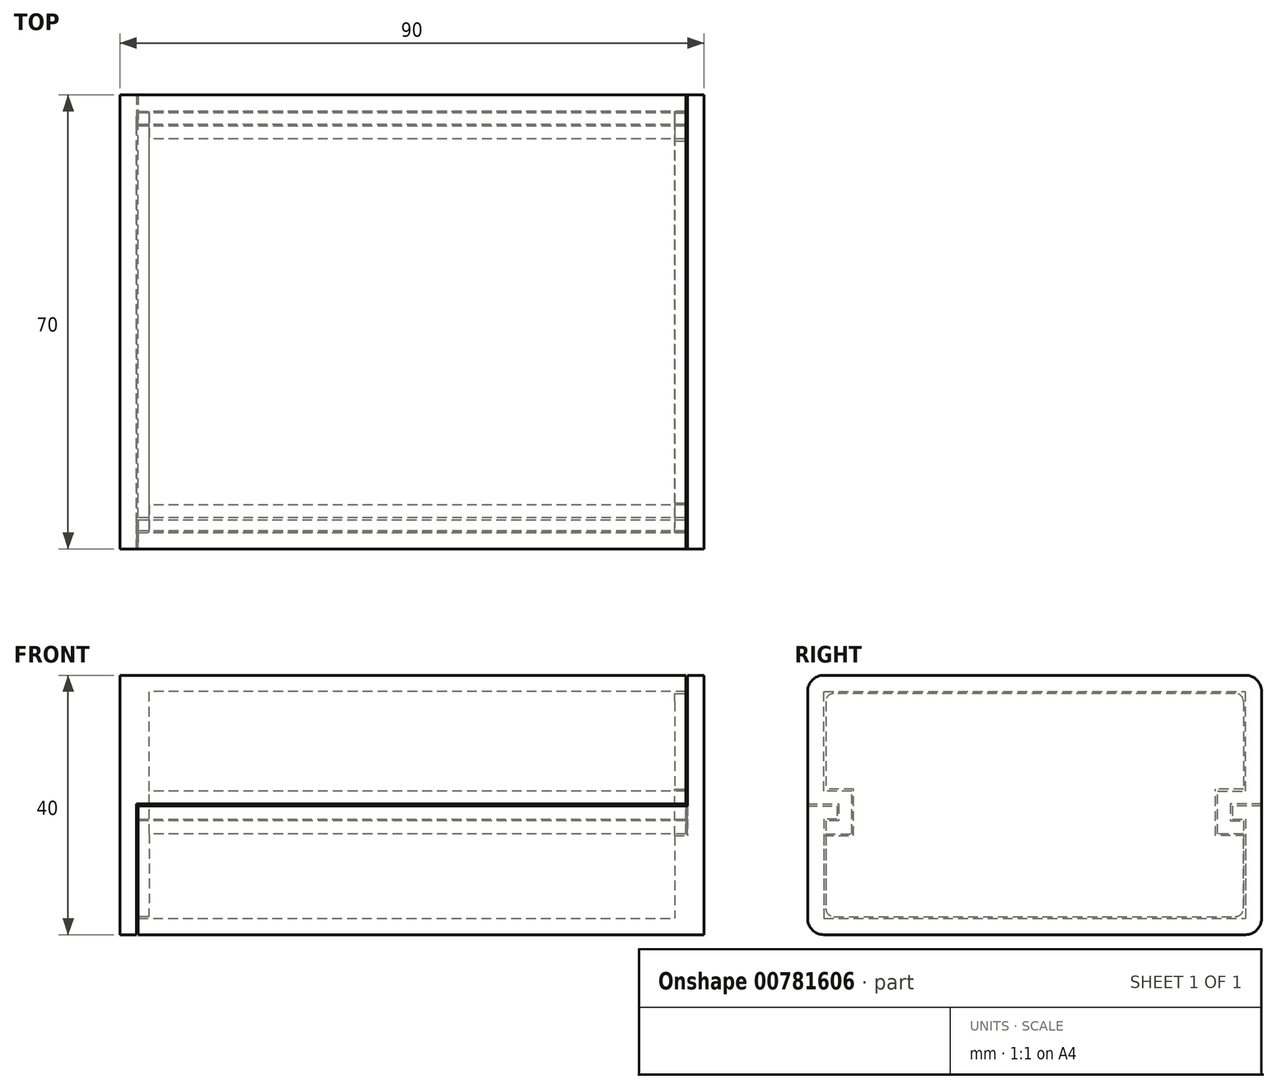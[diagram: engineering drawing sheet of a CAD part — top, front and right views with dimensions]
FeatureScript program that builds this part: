
annotation { "Feature Type Name" : "Feature", "Feature Type Description" : "" }
export const myFeature = defineFeature(function(context is Context, id is Id, definition is map)
    precondition{}
    {
        {
            assignVariable(context, id + "F0", {"name" : "LipSize", "anyValue" : 2});
        }
        {
            assignVariable(context, id + "F1", {"name" : "Thickness", "anyValue" : 2.5});
        }
        {
            var Q0;
            Q0=qCreatedBy(makeId("Top.planeOp"),FACE);
            var sketch = newSketch(context, id + "F2", { "sketchPlane" : qUnion([Q0])});
            skLineSegment(sketch, "E0.bottom", {"start": v(-45, 35) * mm, "end": v(45, 35) * mm});
            skLineSegment(sketch, "E0.top", {"start": v(-45, -35) * mm, "end": v(45, -35) * mm});
            skLineSegment(sketch, "E0.left", {"start": v(-45, 35) * mm, "end": v(-45, -35) * mm});
            skLineSegment(sketch, "E0.right", {"start": v(45, 35) * mm, "end": v(45, -35) * mm});
            skLineSegment(sketch, "E1", {"start": v(-42.5, 35) * mm, "end": v(-42.5, -35) * mm, "construction": true});
            skLineSegment(sketch, "E2", {"start": v(42.5, 35) * mm, "end": v(42.5, -35) * mm, "construction": true});
            skLineSegment(sketch, "E3", {"start": v(42.2, 35) * mm, "end": v(42.2, -35) * mm, "construction": true});
            skLineSegment(sketch, "E4", {"start": v(-42.2, 35) * mm, "end": v(-42.2, -35) * mm, "construction": true});
            skSolve(sketch);
        }
        {
            var Q0;
            Q0=qCreatedBy(makeId("Right.planeOp"),FACE);
            var sketch = newSketch(context, id + "F3", { "sketchPlane" : qUnion([Q0])});
            skLineSegment(sketch, "E5.bottom", {"start": v(-35, 20) * mm, "end": v(35, 20) * mm});
            skLineSegment(sketch, "E5.top", {"start": v(-35, -20) * mm, "end": v(35, -20) * mm});
            skLineSegment(sketch, "E5.left", {"start": v(-35, 20) * mm, "end": v(-35, -20) * mm});
            skLineSegment(sketch, "E5.right", {"start": v(35, 20) * mm, "end": v(35, -20) * mm});
            skLineSegment(sketch, "E6", {"start": v(-35, 0) * mm, "end": v(35, 0) * mm, "construction": true});
            skLineSegment(sketch, "E7", {"start": v(35, 17.5) * mm, "end": v(-35, 17.5) * mm, "construction": true});
            skLineSegment(sketch, "E8", {"start": v(35, 17.2) * mm, "end": v(-35, 17.2) * mm, "construction": true});
            skLineSegment(sketch, "E9", {"start": v(35, -17.5) * mm, "end": v(-35, -17.5) * mm, "construction": true});
            skLineSegment(sketch, "E10", {"start": v(-35, -17.2) * mm, "end": v(35, -17.2) * mm, "construction": true});
            skLineSegment(sketch, "E11", {"start": v(32.5, 17.5) * mm, "end": v(32.5, -17.5) * mm, "construction": true});
            skLineSegment(sketch, "E12", {"start": v(-32.5, 17.5) * mm, "end": v(-32.5, -17.5) * mm, "construction": true});
            skSolve(sketch);
        }
        {
            var Q0;
            Q0=makeQuery(id+"F3.imprint","IMPRINT",FACE,{"disambiguationData":[TD([[makeQuery(id+"F3.imprint","IMPRINT",EDGE,{"derivedFrom":sQuery(id+"F3.wireOp",EDGE,"E5.bottom")}),-1.0]])]});
            var sketch = newSketch(context, id + "F4", { "sketchPlane" : qUnion([Q0])});
            skLineSegment(sketch, "E13", {"start": v(-35, -0.15) * mm, "end": v(-35, -20) * mm});
            skLineSegment(sketch, "E14.0", {"start": v(-35, -20) * mm, "end": v(35, -20) * mm});
            skLineSegment(sketch, "E15.0", {"start": v(-35, 20) * mm, "end": v(35, 20) * mm});
            skLineSegment(sketch, "E16", {"start": v(-35, 20) * mm, "end": v(-35, 0.15) * mm});
            skLineSegment(sketch, "E17", {"start": v(35, 20) * mm, "end": v(35, 0.15) * mm});
            skLineSegment(sketch, "E18", {"start": v(35, -20) * mm, "end": v(35, -0.15) * mm});
            skLineSegment(sketch, "E19", {"start": v(-35, -0.15) * mm, "end": v(-30.5, -0.15) * mm});
            skLineSegment(sketch, "E20", {"start": v(-30.5, -0.15) * mm, "end": v(-30.5, -2.15) * mm});
            skLineSegment(sketch, "E21", {"start": v(-30.5, -2.15) * mm, "end": v(-32.5, -2.15) * mm});
            skLineSegment(sketch, "E22", {"start": v(-32.5, -2.15) * mm, "end": v(-32.5, -17.5) * mm});
            skLineSegment(sketch, "E23", {"start": v(0, 20) * mm, "end": v(0, -20) * mm, "construction": true});
            skLineSegment(sketch, "E24", {"start": v(-32.5, -17.5) * mm, "end": v(32.5, -17.5) * mm});
            skLineSegment(sketch, "E25", {"start": v(-35, 0.15) * mm, "end": v(-30.2, 0.15) * mm});
            skLineSegment(sketch, "E26", {"start": v(-30.2, 0.15) * mm, "end": v(-30.2, -2.45) * mm});
            skLineSegment(sketch, "E27", {"start": v(-30.2, -2.45) * mm, "end": v(-32.2, -2.45) * mm});
            skLineSegment(sketch, "E28", {"start": v(-32.2, -2.45) * mm, "end": v(-32.2, -4.45) * mm});
            skLineSegment(sketch, "E29", {"start": v(-32.2, -4.45) * mm, "end": v(-28.2, -4.45) * mm});
            skLineSegment(sketch, "E30", {"start": v(-28.2, -4.45) * mm, "end": v(-28.2, 2.15) * mm});
            skLineSegment(sketch, "E31", {"start": v(-28.2, 2.15) * mm, "end": v(-32.5, 2.15) * mm});
            skLineSegment(sketch, "E32", {"start": v(-32.5, 2.15) * mm, "end": v(-32.5, 17.5) * mm});
            skLineSegment(sketch, "E33", {"start": v(-32.5, 17.5) * mm, "end": v(32.5, 17.5) * mm});
            skLineSegment(sketch, "E34.MirrorCS", {"start": v(35, -0.15) * mm, "end": v(35, -20) * mm});
            skLineSegment(sketch, "E35.MirrorCS", {"start": v(32.2, -4.45) * mm, "end": v(28.2, -4.45) * mm});
            skLineSegment(sketch, "E36.MirrorCS", {"start": v(32.2, -2.45) * mm, "end": v(32.2, -4.45) * mm});
            skLineSegment(sketch, "E37.MirrorCS", {"start": v(32.5, -2.15) * mm, "end": v(32.5, -17.5) * mm});
            skLineSegment(sketch, "E38.MirrorCS", {"start": v(28.2, 2.15) * mm, "end": v(32.5, 2.15) * mm});
            skLineSegment(sketch, "E39.MirrorCS", {"start": v(30.2, -2.45) * mm, "end": v(32.2, -2.45) * mm});
            skLineSegment(sketch, "E40.MirrorCS", {"start": v(35, -0.15) * mm, "end": v(30.5, -0.15) * mm});
            skLineSegment(sketch, "E41.MirrorCS", {"start": v(30.5, -2.15) * mm, "end": v(32.5, -2.15) * mm});
            skLineSegment(sketch, "E42.MirrorCS", {"start": v(35, 0.15) * mm, "end": v(30.2, 0.15) * mm});
            skLineSegment(sketch, "E43.MirrorCS", {"start": v(30.5, -0.15) * mm, "end": v(30.5, -2.15) * mm});
            skLineSegment(sketch, "E44.MirrorCS", {"start": v(30.2, 0.15) * mm, "end": v(30.2, -2.45) * mm});
            skLineSegment(sketch, "E45.MirrorCS", {"start": v(32.5, 2.15) * mm, "end": v(32.5, 17.5) * mm});
            skLineSegment(sketch, "E46.MirrorCS", {"start": v(28.2, -4.45) * mm, "end": v(28.2, 2.15) * mm});
            skSolve(sketch);
        }
        {
            var Q0;
            Q0=makeQuery(id+"F4.imprint","IMPRINT",FACE,{"disambiguationData":[TD([[makeQuery(id+"F4.imprint","IMPRINT",EDGE,{"derivedFrom":sQuery(id+"F4.wireOp",EDGE,"E15.0")}),-1.0]])]});
            var Q1;
            Q1=sQuery(id+"F2.wireOp",VERTEX,"E3.end");
            var Q2;
            Q2=sQuery(id+"F2.wireOp",VERTEX,"E1.end");
            extrude(context, id + "F5", {"entities" : qUnion([Q0]), "endBound" : BoundingType.UP_TO_VERTEX, "depth" : 25 * mm, "endBoundEntityVertex" : qUnion([Q1]), "offsetDistance" : 25 * mm, "hasSecondDirection" : true, "secondDirectionBound" : BoundingType.UP_TO_VERTEX, "secondDirectionOppositeDirection" : true, "secondDirectionDepth" : 25 * mm, "secondDirectionBoundEntityVertex" : qUnion([Q2])});
        }
        {
            var Q0;
            Q0=makeQuery(id+"F4.imprint","IMPRINT",FACE,{"disambiguationData":[TD([[makeQuery(id+"F4.imprint","IMPRINT",EDGE,{"derivedFrom":sQuery(id+"F4.wireOp",EDGE,"E13")}),1.0]])]});
            var Q1;
            Q1=sQuery(id+"F2.wireOp",VERTEX,"E4.end");
            var Q2;
            Q2=sQuery(id+"F2.wireOp",VERTEX,"E2.end");
            extrude(context, id + "F6", {"entities" : qUnion([Q0]), "endBound" : BoundingType.UP_TO_VERTEX, "oppositeDirection" : true, "depth" : 25 * mm, "endBoundEntityVertex" : qUnion([Q1]), "offsetDistance" : 25 * mm, "hasSecondDirection" : true, "secondDirectionBound" : BoundingType.UP_TO_VERTEX, "secondDirectionOppositeDirection" : false, "secondDirectionDepth" : 25 * mm, "secondDirectionBoundEntityVertex" : qUnion([Q2])});
        }
        {
            var Q0;
            Q0=makeQuery(id+"F5.opExtrude","CAP_FACE",FACE,{"disambiguationData":[OSD([sQuery(id+"F4.wireOp",EDGE,"E15.0"),sQuery(id+"F4.wireOp",EDGE,"E16"),sQuery(id+"F4.wireOp",EDGE,"E25"),sQuery(id+"F4.wireOp",EDGE,"E26"),sQuery(id+"F4.wireOp",EDGE,"E27"),sQuery(id+"F4.wireOp",EDGE,"E28"),sQuery(id+"F4.wireOp",EDGE,"E29"),sQuery(id+"F4.wireOp",EDGE,"E30"),sQuery(id+"F4.wireOp",EDGE,"E31"),sQuery(id+"F4.wireOp",EDGE,"E32"),sQuery(id+"F4.wireOp",EDGE,"E33"),sQuery(id+"F4.wireOp",EDGE,"E17"),sQuery(id+"F4.wireOp",EDGE,"E35.MirrorCS"),sQuery(id+"F4.wireOp",EDGE,"E36.MirrorCS"),sQuery(id+"F4.wireOp",EDGE,"E38.MirrorCS"),sQuery(id+"F4.wireOp",EDGE,"E39.MirrorCS"),sQuery(id+"F4.wireOp",EDGE,"E42.MirrorCS"),sQuery(id+"F4.wireOp",EDGE,"E44.MirrorCS"),sQuery(id+"F4.wireOp",EDGE,"E45.MirrorCS"),sQuery(id+"F4.wireOp",EDGE,"E46.MirrorCS")])],"isStart":true});
            var sketch = newSketch(context, id + "F7", { "sketchPlane" : qUnion([Q0])});
            skLineSegment(sketch, "E47.bottom", {"start": v(-35, 20) * mm, "end": v(35, 20) * mm});
            skLineSegment(sketch, "E47.top", {"start": v(-35, -20) * mm, "end": v(35, -20) * mm});
            skLineSegment(sketch, "E47.left", {"start": v(-35, 20) * mm, "end": v(-35, -20) * mm});
            skLineSegment(sketch, "E47.right", {"start": v(35, 20) * mm, "end": v(35, -20) * mm});
            skSolve(sketch);
        }
        {
            var Q0;
            Q0 = qSketchRegion(id + "F7", true);
            var Q1;
            Q1=sQuery(id+"F2.wireOp",VERTEX,"E0.bottom.start");
            extrude(context, id + "F8", {"entities" : qUnion([Q0]), "operationType" : NewBodyOperationType.ADD, "endBound" : BoundingType.UP_TO_VERTEX, "depth" : 25 * mm, "endBoundEntityVertex" : qUnion([Q1]), "offsetDistance" : 25 * mm});
        }
        {
            var Q0;
            Q0=makeQuery(id+"F6.opExtrude","CAP_FACE",FACE,{"disambiguationData":[OSD([sQuery(id+"F4.wireOp",EDGE,"E13"),sQuery(id+"F4.wireOp",EDGE,"E14.0"),sQuery(id+"F4.wireOp",EDGE,"E19"),sQuery(id+"F4.wireOp",EDGE,"E20"),sQuery(id+"F4.wireOp",EDGE,"E21"),sQuery(id+"F4.wireOp",EDGE,"E22"),sQuery(id+"F4.wireOp",EDGE,"E24"),sQuery(id+"F4.wireOp",EDGE,"E34.MirrorCS"),sQuery(id+"F4.wireOp",EDGE,"E37.MirrorCS"),sQuery(id+"F4.wireOp",EDGE,"E40.MirrorCS"),sQuery(id+"F4.wireOp",EDGE,"E41.MirrorCS"),sQuery(id+"F4.wireOp",EDGE,"E43.MirrorCS")])],"isStart":true});
            var sketch = newSketch(context, id + "F9", { "sketchPlane" : qUnion([Q0])});
            skLineSegment(sketch, "E48.bottom", {"start": v(35, -20) * mm, "end": v(-35, -20) * mm});
            skLineSegment(sketch, "E48.top", {"start": v(35, 20) * mm, "end": v(-35, 20) * mm});
            skLineSegment(sketch, "E48.left", {"start": v(35, -20) * mm, "end": v(35, 20) * mm});
            skLineSegment(sketch, "E48.right", {"start": v(-35, -20) * mm, "end": v(-35, 20) * mm});
            skSolve(sketch);
        }
        {
            var Q0;
            Q0 = qSketchRegion(id + "F9", true);
            var Q1;
            Q1=sQuery(id+"F2.wireOp",VERTEX,"E0.top.end");
            extrude(context, id + "F10", {"entities" : qUnion([Q0]), "operationType" : NewBodyOperationType.ADD, "endBound" : BoundingType.UP_TO_VERTEX, "depth" : 25 * mm, "endBoundEntityVertex" : qUnion([Q1]), "offsetDistance" : 25 * mm});
        }
        {
            var Q0;
            Q0=makeQuery(id+"F8.opExtrude","CAP_FACE",FACE,{"disambiguationData":[OSD([sQuery(id+"F7.wireOp",EDGE,"E47.bottom"),sQuery(id+"F7.wireOp",EDGE,"E47.top"),sQuery(id+"F7.wireOp",EDGE,"E47.left"),sQuery(id+"F7.wireOp",EDGE,"E47.right")])],"isStart":true});
            var sketch = newSketch(context, id + "F11", { "sketchPlane" : qUnion([Q0])});
            skLineSegment(sketch, "E49", {"start": v(-32.2, -4.45) * mm, "end": v(-32.2, -17.2) * mm});
            skLineSegment(sketch, "E50", {"start": v(-32.2, -17.2) * mm, "end": v(32.2, -17.2) * mm});
            skLineSegment(sketch, "E51", {"start": v(32.2, -17.2) * mm, "end": v(32.2, -4.45) * mm});
            skSolve(sketch);
        }
        {
            var Q0;
            Q0=makeQuery(id+"F11.imprint","IMPRINT",FACE,{"disambiguationData":[TD([[makeQuery(id+"F11.imprint","IMPRINT",EDGE,{"derivedFrom":sQuery(id+"F11.wireOp",EDGE,"E49")}),1.0]])]});
            extrude(context, id + "F12", {"entities" : qUnion([Q0]), "operationType" : NewBodyOperationType.ADD, "depth" : (getVariable(context, 'LipSize')) * mm, "offsetDistance" : 25 * mm});
        }
        {
            var Q0;
            Q0=makeQuery(id+"F10.opExtrude","CAP_FACE",FACE,{"disambiguationData":[OSD([sQuery(id+"F9.wireOp",EDGE,"E48.bottom"),sQuery(id+"F9.wireOp",EDGE,"E48.top"),sQuery(id+"F9.wireOp",EDGE,"E48.left"),sQuery(id+"F9.wireOp",EDGE,"E48.right")])],"isStart":true});
            var sketch = newSketch(context, id + "F13", { "sketchPlane" : qUnion([Q0])});
            skLineSegment(sketch, "E52.bottom", {"start": v(-32.2, 17.2) * mm, "end": v(32.2, 17.2) * mm});
            skLineSegment(sketch, "E52.top", {"start": v(-32.2, 2.45) * mm, "end": v(-27.9, 2.45) * mm});
            skLineSegment(sketch, "E52.left", {"start": v(-32.2, 17.2) * mm, "end": v(-32.2, 2.45) * mm});
            skLineSegment(sketch, "E52.right", {"start": v(32.2, 17.2) * mm, "end": v(32.2, 2.45) * mm});
            skLineSegment(sketch, "E53", {"start": v(-32.5, -4.75) * mm, "end": v(-27.9, -4.75) * mm});
            skLineSegment(sketch, "E54", {"start": v(-27.9, -4.75) * mm, "end": v(-27.9, 2.45) * mm});
            skLineSegment(sketch, "E55.MirrorCS", {"start": v(27.9, -4.75) * mm, "end": v(27.9, 2.45) * mm});
            skLineSegment(sketch, "E56.MirrorCS", {"start": v(32.5, -4.75) * mm, "end": v(27.9, -4.75) * mm});
            skLineSegment(sketch, "E57.trimOffspring", {"start": v(27.9, 2.45) * mm, "end": v(32.2, 2.45) * mm});
            skSolve(sketch);
        }
        {
            var Q0;
            Q0=makeQuery(id+"F13.imprint","IMPRINT",FACE,{"disambiguationData":[TD([[makeQuery(id+"F13.imprint","IMPRINT",EDGE,{"derivedFrom":sQuery(id+"F13.wireOp",EDGE,"E52.bottom")}),-1.0]])]});
            extrude(context, id + "F14", {"entities" : qUnion([Q0]), "operationType" : NewBodyOperationType.ADD, "depth" : (getVariable(context, 'LipSize')) * mm, "offsetDistance" : 25 * mm});
        }
        {
            var Q0;
            Q0=makeQuery(id+"F8.boolean.opBoolean","MERGE",EDGE,{"derivedFrom":[makeQuery(id+"F5.opExtrude","TWEAK_EDGE",EDGE,{"derivedFrom":[makeQuery(id+"F4.imprint","IMPRINT",EDGE,{"derivedFrom":sQuery(id+"F4.wireOp",EDGE,"E15.0")}),makeQuery(id+"F4.imprint","IMPRINT",EDGE,{"derivedFrom":sQuery(id+"F4.wireOp",EDGE,"E16")})]}),makeQuery(id+"F8.opExtrude","SWEPT_EDGE",EDGE,{"disambiguationData":[OSD([sQuery(id+"F7.wireOp",EDGE,"E47.bottom"),sQuery(id+"F7.wireOp",EDGE,"E47.right")])]})]});
            var Q1;
            Q1=makeQuery(id+"F8.boolean.opBoolean","MERGE",EDGE,{"derivedFrom":[makeQuery(id+"F5.opExtrude","TWEAK_EDGE",EDGE,{"derivedFrom":[makeQuery(id+"F4.imprint","IMPRINT",EDGE,{"derivedFrom":sQuery(id+"F4.wireOp",EDGE,"E15.0")}),makeQuery(id+"F4.imprint","IMPRINT",EDGE,{"derivedFrom":sQuery(id+"F4.wireOp",EDGE,"E17")})]}),makeQuery(id+"F8.opExtrude","SWEPT_EDGE",EDGE,{"disambiguationData":[OSD([sQuery(id+"F7.wireOp",EDGE,"E47.bottom"),sQuery(id+"F7.wireOp",EDGE,"E47.left")])]})]});
            var Q2;
            Q2=makeQuery(id+"F10.boolean.opBoolean","MERGE",EDGE,{"derivedFrom":[makeQuery(id+"F6.opExtrude","TWEAK_EDGE",EDGE,{"derivedFrom":[makeQuery(id+"F4.imprint","IMPRINT",EDGE,{"derivedFrom":sQuery(id+"F4.wireOp",EDGE,"E13")}),makeQuery(id+"F4.imprint","IMPRINT",EDGE,{"derivedFrom":sQuery(id+"F4.wireOp",EDGE,"E14.0")})]}),makeQuery(id+"F10.opExtrude","SWEPT_EDGE",EDGE,{"disambiguationData":[OSD([sQuery(id+"F9.wireOp",EDGE,"E48.bottom"),sQuery(id+"F9.wireOp",EDGE,"E48.right")])]})]});
            var Q3;
            Q3=makeQuery(id+"F8.opExtrude","SWEPT_EDGE",EDGE,{"disambiguationData":[OSD([sQuery(id+"F7.wireOp",EDGE,"E47.top"),sQuery(id+"F7.wireOp",EDGE,"E47.right")])]});
            var Q4;
            Q4=makeQuery(id+"F10.opExtrude","SWEPT_EDGE",EDGE,{"disambiguationData":[OSD([sQuery(id+"F9.wireOp",EDGE,"E48.top"),sQuery(id+"F9.wireOp",EDGE,"E48.right")])]});
            var Q5;
            Q5=makeQuery(id+"F10.opExtrude","SWEPT_EDGE",EDGE,{"disambiguationData":[OSD([sQuery(id+"F9.wireOp",EDGE,"E48.top"),sQuery(id+"F9.wireOp",EDGE,"E48.left")])]});
            var Q6;
            Q6=makeQuery(id+"F8.opExtrude","SWEPT_EDGE",EDGE,{"disambiguationData":[OSD([sQuery(id+"F7.wireOp",EDGE,"E47.top"),sQuery(id+"F7.wireOp",EDGE,"E47.left")])]});
            var Q7;
            Q7=makeQuery(id+"F10.boolean.opBoolean","MERGE",EDGE,{"derivedFrom":[makeQuery(id+"F6.opExtrude","TWEAK_EDGE",EDGE,{"derivedFrom":[makeQuery(id+"F4.imprint","IMPRINT",EDGE,{"derivedFrom":sQuery(id+"F4.wireOp",EDGE,"E14.0")}),makeQuery(id+"F4.imprint","IMPRINT",EDGE,{"derivedFrom":sQuery(id+"F4.wireOp",EDGE,"E34.MirrorCS")})]}),makeQuery(id+"F10.opExtrude","SWEPT_EDGE",EDGE,{"disambiguationData":[OSD([sQuery(id+"F9.wireOp",EDGE,"E48.bottom"),sQuery(id+"F9.wireOp",EDGE,"E48.left")])]})]});
            fillet(context, id + "F15", {"entities" : qUnion([Q0, Q1, Q2, Q3, Q4, Q5, Q6, Q7]), "radius" : (getVariable(context, 'Thickness')) * mm, "tangentPropagation" : true, "allowEdgeOverflow" : false});
        }
        {
            var Q0;
            Q0=makeQuery(id+"F12.opExtrude","SWEPT_EDGE",EDGE,{"disambiguationData":[OSD([sQuery(id+"F11.wireOp",EDGE,"E49"),sQuery(id+"F11.wireOp",EDGE,"E50")])]});
            var Q1;
            Q1=makeQuery(id+"F12.opExtrude","SWEPT_EDGE",EDGE,{"disambiguationData":[OSD([sQuery(id+"F11.wireOp",EDGE,"E50"),sQuery(id+"F11.wireOp",EDGE,"E51")])]});
            var Q2;
            Q2=makeQuery(id+"F5.opExtrude","TWEAK_EDGE",EDGE,{"derivedFrom":[makeQuery(id+"F4.imprint","IMPRINT",EDGE,{"derivedFrom":sQuery(id+"F4.wireOp",EDGE,"E32")}),makeQuery(id+"F4.imprint","IMPRINT",EDGE,{"derivedFrom":sQuery(id+"F4.wireOp",EDGE,"E33")})]});
            var Q3;
            Q3=makeQuery(id+"F5.opExtrude","TWEAK_EDGE",EDGE,{"derivedFrom":[makeQuery(id+"F4.imprint","IMPRINT",EDGE,{"derivedFrom":sQuery(id+"F4.wireOp",EDGE,"E33")}),makeQuery(id+"F4.imprint","IMPRINT",EDGE,{"derivedFrom":sQuery(id+"F4.wireOp",EDGE,"E45.MirrorCS")})]});
            var Q4;
            Q4=makeQuery(id+"F6.opExtrude","TWEAK_EDGE",EDGE,{"derivedFrom":[makeQuery(id+"F4.imprint","IMPRINT",EDGE,{"derivedFrom":sQuery(id+"F4.wireOp",EDGE,"E22")}),makeQuery(id+"F4.imprint","IMPRINT",EDGE,{"derivedFrom":sQuery(id+"F4.wireOp",EDGE,"E24")})]});
            var Q5;
            Q5=makeQuery(id+"F6.opExtrude","TWEAK_EDGE",EDGE,{"derivedFrom":[makeQuery(id+"F4.imprint","IMPRINT",EDGE,{"derivedFrom":sQuery(id+"F4.wireOp",EDGE,"E24")}),makeQuery(id+"F4.imprint","IMPRINT",EDGE,{"derivedFrom":sQuery(id+"F4.wireOp",EDGE,"E37.MirrorCS")})]});
            var Q6;
            Q6=makeQuery(id+"F14.opExtrude","SWEPT_EDGE",EDGE,{"disambiguationData":[OSD([sQuery(id+"F13.wireOp",EDGE,"E52.bottom"),sQuery(id+"F13.wireOp",EDGE,"E52.left")])]});
            var Q7;
            Q7=makeQuery(id+"F14.opExtrude","SWEPT_EDGE",EDGE,{"disambiguationData":[OSD([sQuery(id+"F13.wireOp",EDGE,"E52.bottom"),sQuery(id+"F13.wireOp",EDGE,"E52.right")])]});
            fillet(context, id + "F16", {"entities" : qUnion([Q0, Q1, Q2, Q3, Q4, Q5, Q6, Q7]), "radius" : (getVariable(context, 'Thickness') / 2) * mm, "tangentPropagation" : true, "allowEdgeOverflow" : false});
        }
    });
